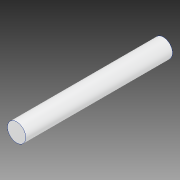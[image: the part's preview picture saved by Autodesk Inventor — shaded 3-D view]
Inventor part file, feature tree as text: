
AUTODESK INVENTOR PART (.ipt)
format: ipt  version: 2020 (Build 240168000, 168)  size: 77,312 bytes
history: native  units: mm
features: extrude x1, sketch x1
ambient origin geometry x8: Origin, YZ Plane, XZ Plane, XY Plane, X Axis, Y Axis, Z Axis, Center Point
bodies: Solid1 (feature_tree)
feature tree (2):
  extrude  "Extrusion1"  Depth=76.0mm TaperAngle=0.0deg
  sketch  "Sketch1"  dims[d0=9.525mm d1=76.0mm d2=0.0mm]
